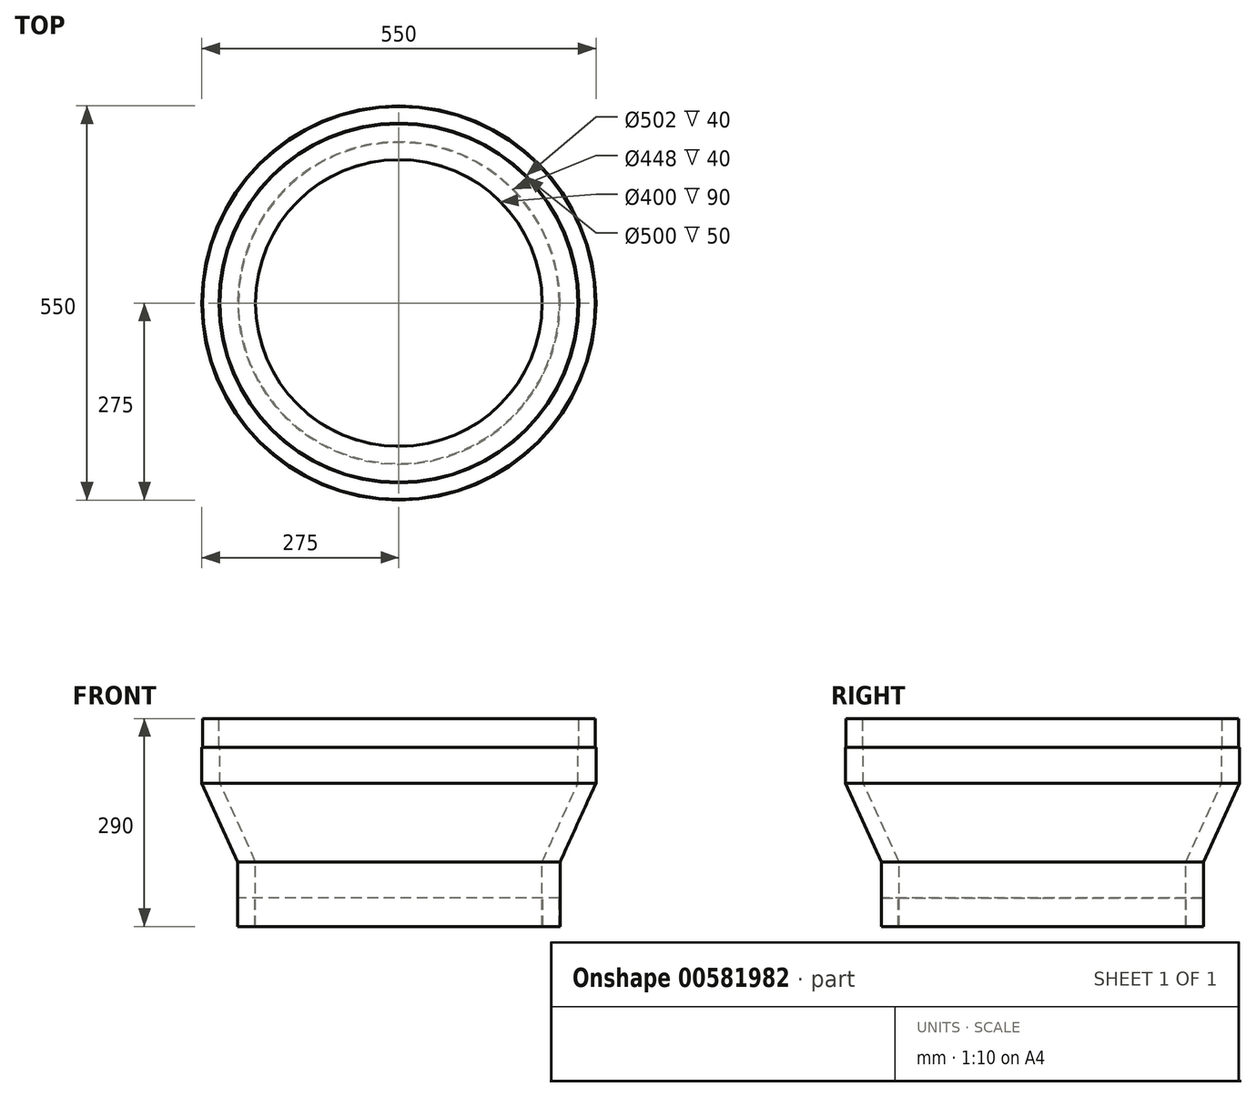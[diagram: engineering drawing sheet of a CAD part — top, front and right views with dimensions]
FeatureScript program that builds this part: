
annotation { "Feature Type Name" : "Feature", "Feature Type Description" : "" }
export const myFeature = defineFeature(function(context is Context, id is Id, definition is map)
    precondition{}
    {
        {
            var Q0;
            Q0=qCreatedBy(makeId("Front.planeOp"),FACE);
            var sketch = newSketch(context, id + "F0", { "sketchPlane" : qUnion([Q0])});
            skLineSegment(sketch, "E0", {"start": v(0, 433.08) * mm, "end": v(0, -434.74) * mm, "construction": true});
            skLineSegment(sketch, "E1", {"start": v(-200, -69.87) * mm, "end": v(-200, 20.13) * mm});
            skLineSegment(sketch, "E2", {"start": v(-200, -69.87) * mm, "end": v(-201, -69.87) * mm});
            skLineSegment(sketch, "E3", {"start": v(-201, -69.87) * mm, "end": v(-201, -29.87) * mm});
            skLineSegment(sketch, "E4", {"start": v(-201, -29.87) * mm, "end": v(-224, -29.87) * mm});
            skLineSegment(sketch, "E5", {"start": v(-224, -29.87) * mm, "end": v(-224, -69.87) * mm});
            skLineSegment(sketch, "E6", {"start": v(-224, -69.87) * mm, "end": v(-225, -69.87) * mm});
            skLineSegment(sketch, "E7", {"start": v(-225, -69.87) * mm, "end": v(-225, 20.13) * mm});
            skLineSegment(sketch, "E8", {"start": v(-274, 220.13) * mm, "end": v(-251, 220.13) * mm});
            skLineSegment(sketch, "E9", {"start": v(-251, 220.13) * mm, "end": v(-251, 180.13) * mm});
            skLineSegment(sketch, "E10", {"start": v(-251, 180.13) * mm, "end": v(-250, 180.13) * mm});
            skLineSegment(sketch, "E11", {"start": v(-250, 180.13) * mm, "end": v(-250, 130.13) * mm});
            skLineSegment(sketch, "E12", {"start": v(-274, 220.13) * mm, "end": v(-274, 180.13) * mm});
            skLineSegment(sketch, "E13", {"start": v(-274, 180.13) * mm, "end": v(-275, 180.13) * mm});
            skLineSegment(sketch, "E14", {"start": v(-275, 180.13) * mm, "end": v(-275, 130.13) * mm});
            skLineSegment(sketch, "E15", {"start": v(-250, 130.13) * mm, "end": v(-200, 20.13) * mm});
            skLineSegment(sketch, "E16", {"start": v(-275, 130.13) * mm, "end": v(-225, 20.13) * mm});
            skSolve(sketch);
        }
        {
            var Q0;
            Q0=qSketchRegion(id+"F0",true);
            var Q1;
            Q1=sQuery(id+"F0.wireOp",EDGE,"E0");
            revolve(context, id + "F1", {"entities" : qUnion([Q0]), "axis" : qUnion([Q1]), "revolveType" : RevolveType.FULL});
        }
    });
